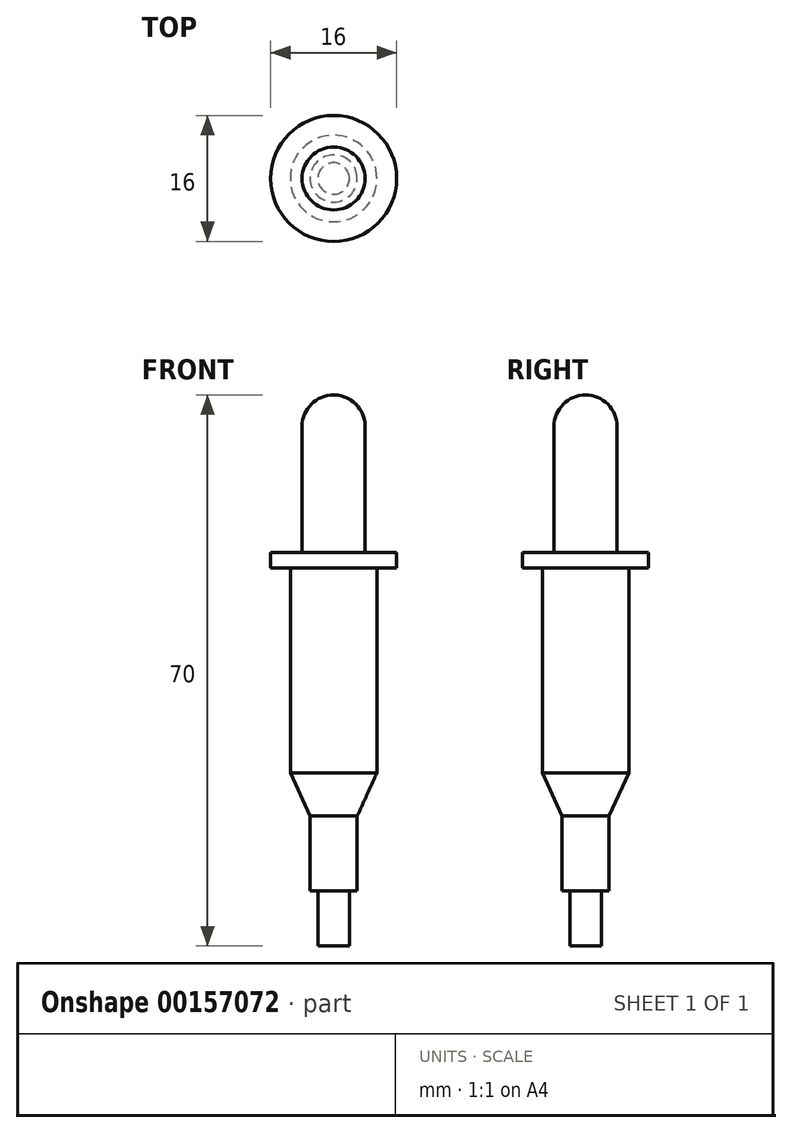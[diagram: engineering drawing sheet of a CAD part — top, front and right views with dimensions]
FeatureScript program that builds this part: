
annotation { "Feature Type Name" : "Feature", "Feature Type Description" : "" }
export const myFeature = defineFeature(function(context is Context, id is Id, definition is map)
    precondition{}
    {
        {
            var Q0;
            Q0=qCreatedBy(makeId("Front.planeOp"),FACE);
            var sketch = newSketch(context, id + "F0", { "sketchPlane" : qUnion([Q0])});
            skLineSegment(sketch, "E0", {"start": v(0, 0) * mm, "end": v(0, 70) * mm, "construction": true});
            skLineSegment(sketch, "E1", {"start": v(-2, 0) * mm, "end": v(-2, 7) * mm});
            skLineSegment(sketch, "E2", {"start": v(-3, 7) * mm, "end": v(-3, 16.5) * mm});
            skLineSegment(sketch, "E3", {"start": v(-3, 16.5) * mm, "end": v(-5.5, 22) * mm});
            skLineSegment(sketch, "E4", {"start": v(-5.5, 22) * mm, "end": v(-5.5, 48) * mm});
            skLineSegment(sketch, "E5", {"start": v(-8, 48) * mm, "end": v(-8, 50) * mm});
            skLineSegment(sketch, "E6", {"start": v(-4, 50) * mm, "end": v(-4, 66) * mm});
            skLineSegment(sketch, "E7", {"start": v(-2, 0) * mm, "end": v(0, 0) * mm});
            skLineSegment(sketch, "E8", {"start": v(-3, 7) * mm, "end": v(-2, 7) * mm});
            skLineSegment(sketch, "E9", {"start": v(-8, 48) * mm, "end": v(-5.5, 48) * mm});
            skLineSegment(sketch, "E10", {"start": v(-8, 50) * mm, "end": v(-4, 50) * mm});
            skArc(sketch, "E11", {"start": v(0, 70) * mm, "mid": v(-2.83, 68.83) * mm, "end": v(-4, 66) * mm});
            skPoint(sketch, "E11.second.point", {"position": v(-4, 66) * mm});
            skPoint(sketch, "E11.third.point", {"position": v(0, 62) * mm});
            skLineSegment(sketch, "E12", {"start": v(0, 70) * mm, "end": v(0, 0) * mm});
            skSolve(sketch);
        }
        {
            var Q0;
            Q0 = qSketchRegion(id + "F0", true);
            var Q1;
            Q1=sQuery(id+"F0.wireOp",EDGE,"E12");
            revolve(context, id + "F1", {"entities" : qUnion([Q0]), "axis" : qUnion([Q1]), "revolveType" : RevolveType.FULL});
        }
    });
